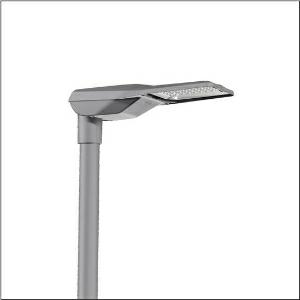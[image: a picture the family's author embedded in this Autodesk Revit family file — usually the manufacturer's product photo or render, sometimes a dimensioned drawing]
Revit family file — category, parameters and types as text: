
# Revit family: streetlight_sl_21_iq_mini___p0_8ab_5xe2r31d08hb_f27f
name_source: partatom
category: Lighting Fixtures
units: mm (PartAtom-declared; Revit-internal decimal feet)

## family parameters
Cut with Voids When Loaded = No
Host = Face
Light Source = No
Part Type = Normal
Room Calculation Point = No
Round Connector Dimension = Use Diameter
Shared = No

## types (1)
- --- (1 x LED, 8210 lm, 70.9 W, 3000K)
    Apparent Load = 71 VA
    CIE Flux Codes = 36 71 98 100 100
    Color Rendering = 70
    Color Temperature = 3000K
    Default Elevation = 1800 mm
    Description = Streetlight SL 21 iQ mini, mast luminaire, primary light control with lens, of PMMA, primary optical cover: cover, of toughened safety glass, transparent, light distribution: P0.8aB, light emission: direct distribution, primary light characteristic: asymmetric, installation type: post-top, side-entry, LED, High Power LED, rated luminous flux: 8.210lm, luminous efficacy: 116lm/W, light colour: 730, colour temperature: 3000K, control gear: iQ-Comfort, control: pre-setting: linear dimming characteristic, Auto-Match, Temp-Guard, Lumen-Switch, Night-Set, Smart-Wire, Light-Fading, Desk-Remote (wireless, voltage-free reading and setting of iQ features in the workshop via application-optimized NFC function/RFID function), optimised constant luminous flux control (CLO 2.0), mains connection: 220..240V, AC, 50/60Hz, start of lifetime: 71W, end of service life: 75W, reduction: 31W, luminaire housing, of diecast aluminium, powder-coated, SITECO metallic grey (DB 702S), corrosivity category C5 high according to DIN EN ISO 12944, please order mast flange separately, inclination adjustable: 0°, 5°, 10°, 15°, sealing non-destructively replaceable, multi-level sealing system, length: 628mm, width: 235mm, height: 110mm, mast flange for spigot size: 42mm (side-entry): 5XC10008XM4, 60/48mm (side-entry/post-top): 5XC10108XM2, 76/60mm (side-entry/post-top): 5XC10108XM1, mounting height: 4..8m, protection rating (complete): IP66, insulation class (complete): insulation class II (safety insulation), certification: CE, ENEC, ENEC+, VDE, impact resistance: IK10, permissible operating ambient temperature for outdoor applications: -40..+50°C, standard-compliant lighting for roads and squares, packaging unit: 1 piece

Light Distribution: P0.8aB
    Height = 110 mm
    Lamp = 1 x LED
    Lamp Light Flux = 8210 lm
    Lamp Power = 70.9 W
    Lamp count = 1
    Length = 625 mm
    Luminous efficacy = 116 lm/W
    Manufacturer = Siteco
    ModVariant = No
    Model = 5XE2R31D08HB
    Number of Poles = 1
    OnlyDefault = Yes
    Power Factor = 1
    Product Name = Streetlight SL 21 iQ mini | P0.8aB
    Product group = mast luminaire | pylon top
    ProductGroupID = 6100
    Protection Class = Protection class II
    Protection Degree = IP 66
    RLX_Detail_Level = 1
    RLX_Emergency_Light_Flux = 0 lm
    RLX_Emergency_Type = 0
    RLX_Emergency_Type_DB = No
    RlxData = <blob elided: 91785 chars, md5=62a19f05>
    Socket = socket
    Standby Power = 0 W
    System Light Flux = 8210 lm
    System Power = 71 W
    Type Comments = factory setting: luminous flux: 100 % | dim-lin: 254 | 711 mA
    Type Image = l_1003519.jpg
    URL = http://relux.com
    VarID = @adj_082225
    Voltage = 0 V
    Weight = 0.00 kg
    Width = 234 mm

## geometry (parser evidence)
native form markers: Blend x4, Sweep x12
no freeform markers — native parametric forms only
